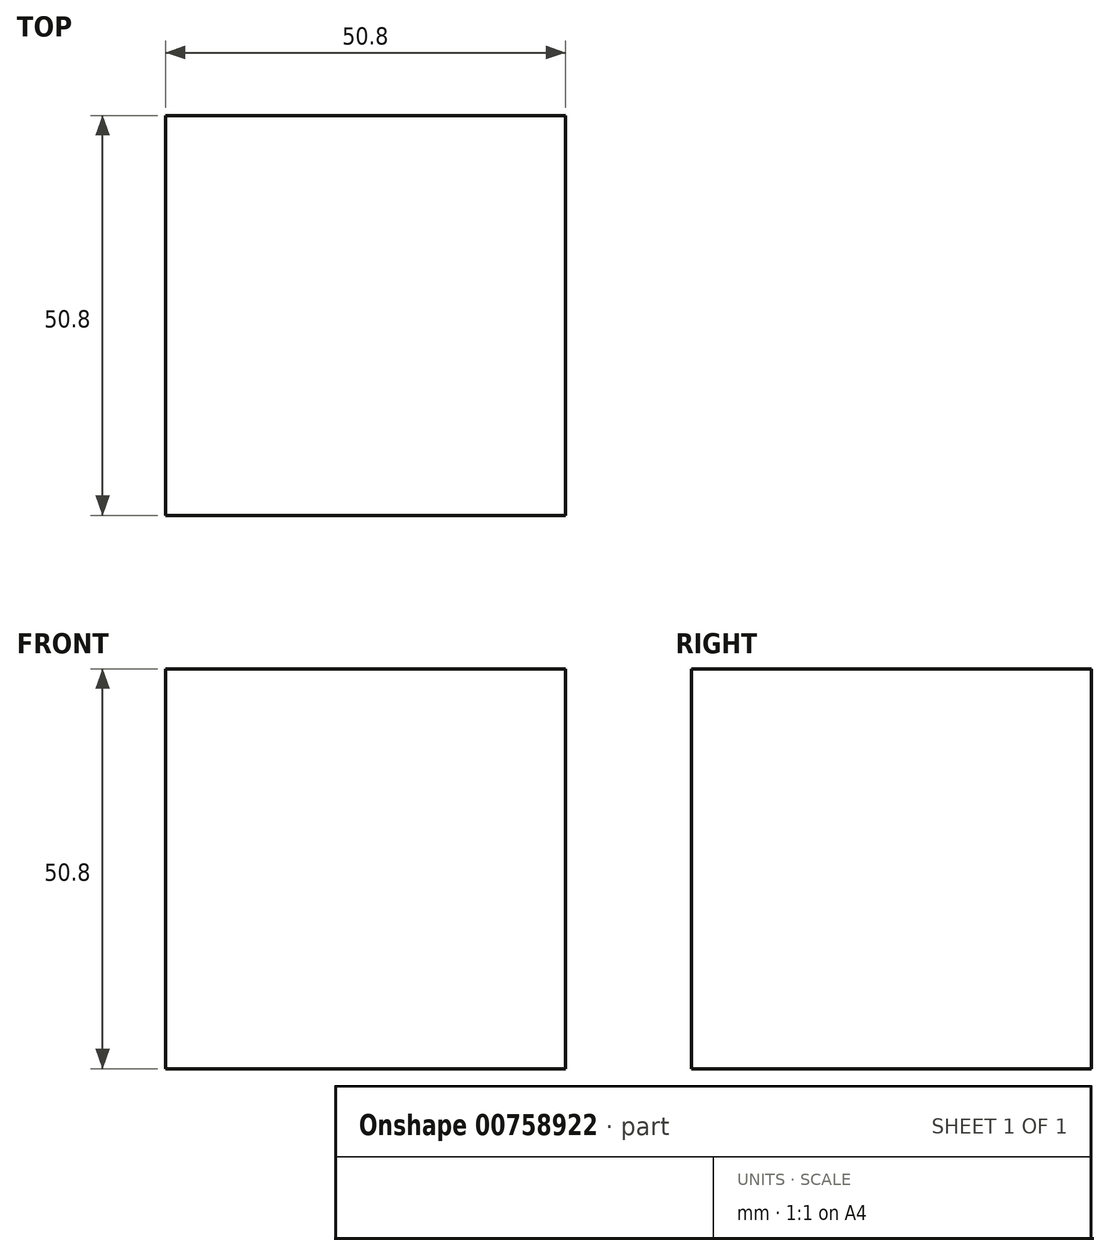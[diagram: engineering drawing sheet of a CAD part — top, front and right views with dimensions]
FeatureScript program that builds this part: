
annotation { "Feature Type Name" : "Feature", "Feature Type Description" : "" }
export const myFeature = defineFeature(function(context is Context, id is Id, definition is map)
    precondition{}
    {
        {
            var Q0;
            Q0=qCreatedBy(makeId("Top.planeOp"),FACE);
            var sketch = newSketch(context, id + "F0", { "sketchPlane" : qUnion([Q0])});
            skLineSegment(sketch, "E0.bottom", {"start": v(-25.24, 32.87) * mm, "end": v(25.56, 32.87) * mm});
            skLineSegment(sketch, "E0.top", {"start": v(-25.24, -17.93) * mm, "end": v(25.56, -17.93) * mm});
            skLineSegment(sketch, "E0.left", {"start": v(-25.24, 32.87) * mm, "end": v(-25.24, -17.93) * mm});
            skLineSegment(sketch, "E0.right", {"start": v(25.56, 32.87) * mm, "end": v(25.56, -17.93) * mm});
            skSolve(sketch);
        }
        {
            var Q0;
            Q0=makeQuery(id+"F0.imprint","IMPRINT",FACE,{"disambiguationData":[TD([[makeQuery(id+"F0.imprint","IMPRINT",EDGE,{"derivedFrom":sQuery(id+"F0.wireOp",EDGE,"E0.bottom")}),-1.0]])]});
            extrude(context, id + "F1", {"entities" : qUnion([Q0]), "depth" : 50.8 * mm, "offsetDistance" : 25.4 * mm});
        }
    });
